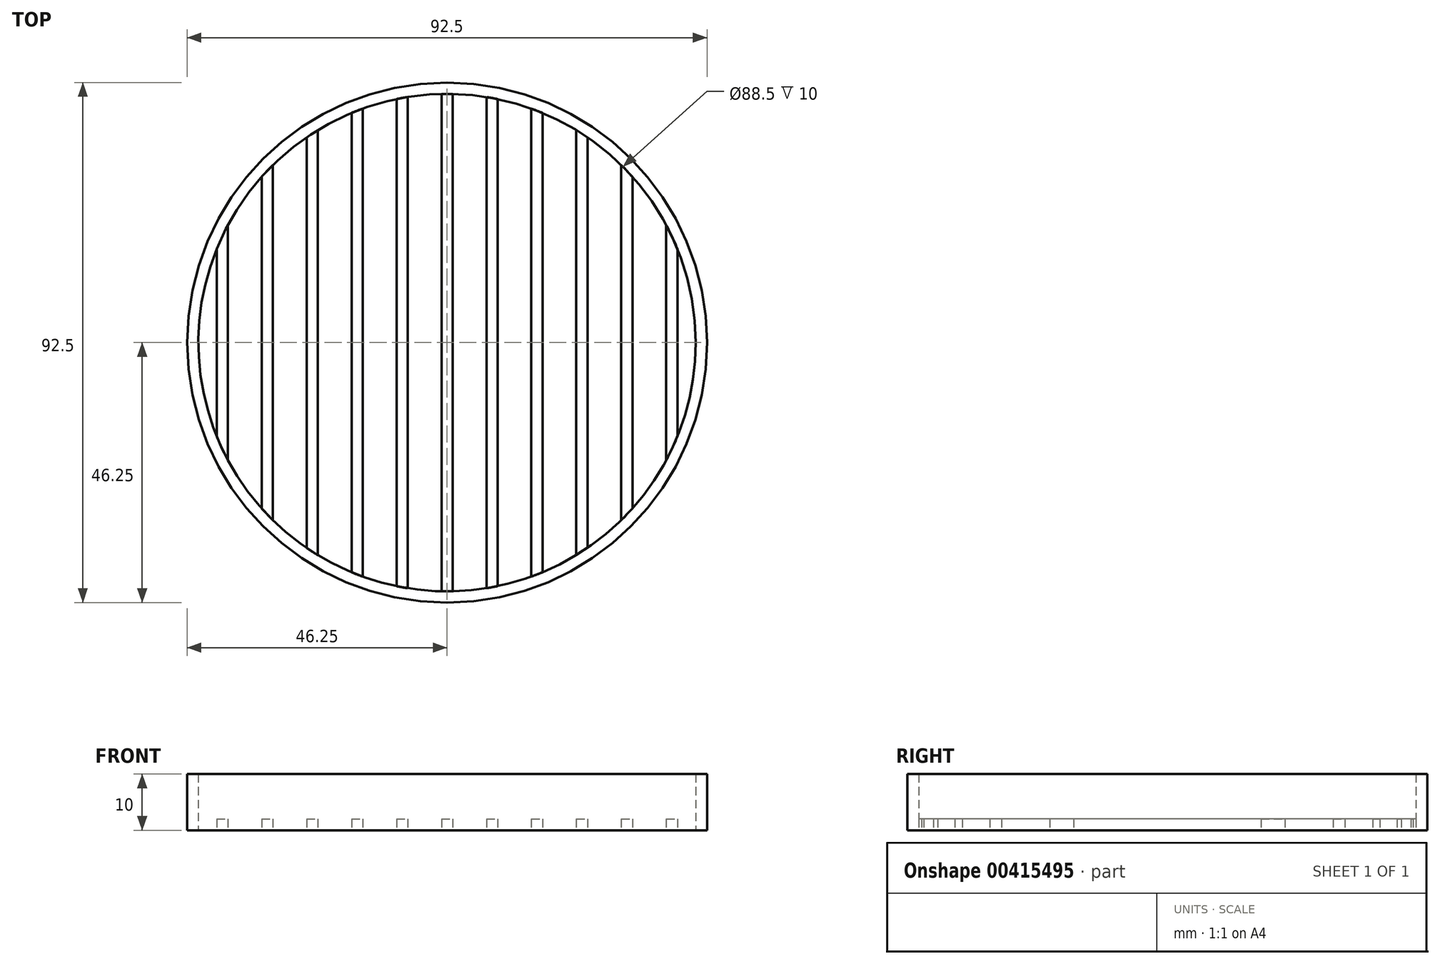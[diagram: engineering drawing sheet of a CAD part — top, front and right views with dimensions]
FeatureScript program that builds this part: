
annotation { "Feature Type Name" : "Feature", "Feature Type Description" : "" }
export const myFeature = defineFeature(function(context is Context, id is Id, definition is map)
    precondition{}
    {
        {
            var Q0;
            Q0=qCreatedBy(makeId("Top.planeOp"),FACE);
            var sketch = newSketch(context, id + "F0", { "sketchPlane" : qUnion([Q0])});
            skCircle(sketch, "E0", {"center": v(0, 0) * mm, "radius": 44.25 * mm});
            skCircle(sketch, "E1", {"center": v(0, 0) * mm, "radius": 46.25 * mm});
            skLineSegment(sketch, "E2", {"start": v(44.25, 0) * mm, "end": v(46.25, 0) * mm, "construction": true});
            skLineSegment(sketch, "E3", {"start": v(0, 44.25) * mm, "end": v(0, -44.25) * mm});
            skLineSegment(sketch, "E4", {"start": v(-1, 46.24) * mm, "end": v(-1, -46.24) * mm});
            skLineSegment(sketch, "E5", {"start": v(1, 38.24) * mm, "end": v(1, -46.24) * mm});
            skLineSegment(sketch, "E6", {"start": v(-1, 6.77) * mm, "end": v(0, 6.77) * mm, "construction": true});
            skLineSegment(sketch, "E7", {"start": v(0, 6.77) * mm, "end": v(1, 6.77) * mm, "construction": true});
            skLineSegment(sketch, "E8", {"start": v(-7, 45.72) * mm, "end": v(-7, -45.72) * mm});
            skLineSegment(sketch, "E9", {"start": v(-7, 0) * mm, "end": v(-1, 0) * mm, "construction": true});
            skLineSegment(sketch, "E10", {"start": v(-9, 45.37) * mm, "end": v(-9, -45.37) * mm});
            skLineSegment(sketch, "E11", {"start": v(-9, 0) * mm, "end": v(-7, 0) * mm, "construction": true});
            skLineSegment(sketch, "E12", {"start": v(-15, 43.75) * mm, "end": v(-15, -43.75) * mm});
            skLineSegment(sketch, "E13", {"start": v(-17, 43.01) * mm, "end": v(-17, -43.01) * mm});
            skLineSegment(sketch, "E14", {"start": v(-15, 0) * mm, "end": v(-9, 0) * mm, "construction": true});
            skLineSegment(sketch, "E15", {"start": v(-17, 0) * mm, "end": v(-15, 0) * mm, "construction": true});
            skLineSegment(sketch, "E16", {"start": v(-23, 40.13) * mm, "end": v(-23, -40.13) * mm});
            skLineSegment(sketch, "E17", {"start": v(-25, 38.91) * mm, "end": v(-25, -38.91) * mm});
            skLineSegment(sketch, "E18", {"start": v(-23, 0) * mm, "end": v(-17, 0) * mm, "construction": true});
            skLineSegment(sketch, "E19", {"start": v(-25, 0) * mm, "end": v(-23, 0) * mm, "construction": true});
            skLineSegment(sketch, "E20", {"start": v(-31, 34.32) * mm, "end": v(-31, -34.32) * mm});
            skLineSegment(sketch, "E21", {"start": v(-33, 32.4) * mm, "end": v(-33, -32.4) * mm});
            skLineSegment(sketch, "E22", {"start": v(-31, 0) * mm, "end": v(-25, 0) * mm, "construction": true});
            skLineSegment(sketch, "E23", {"start": v(-33, 0) * mm, "end": v(-31, 0) * mm, "construction": true});
            skLineSegment(sketch, "E24", {"start": v(7, 45.72) * mm, "end": v(7, -45.72) * mm});
            skLineSegment(sketch, "E25", {"start": v(9, 45.37) * mm, "end": v(9, -45.37) * mm});
            skLineSegment(sketch, "E26", {"start": v(1, 0) * mm, "end": v(7, 0) * mm, "construction": true});
            skPoint(sketch, "E26.startSnap0", {"position": v(7, 0) * mm});
            skLineSegment(sketch, "E27", {"start": v(7, 0) * mm, "end": v(9, 0) * mm, "construction": true});
            skLineSegment(sketch, "E28", {"start": v(15, 43.75) * mm, "end": v(15, -43.75) * mm});
            skLineSegment(sketch, "E29", {"start": v(17, 43.01) * mm, "end": v(17, -43.01) * mm});
            skLineSegment(sketch, "E30", {"start": v(9, 0) * mm, "end": v(15, 0) * mm, "construction": true});
            skLineSegment(sketch, "E31", {"start": v(15, 0) * mm, "end": v(17, 0) * mm, "construction": true});
            skLineSegment(sketch, "E32", {"start": v(23, 40.13) * mm, "end": v(23, -40.13) * mm});
            skLineSegment(sketch, "E33", {"start": v(25, 38.91) * mm, "end": v(25, -38.91) * mm});
            skLineSegment(sketch, "E34", {"start": v(17, 0) * mm, "end": v(23, 0) * mm, "construction": true});
            skLineSegment(sketch, "E35", {"start": v(23, 0) * mm, "end": v(25, 0) * mm, "construction": true});
            skLineSegment(sketch, "E36", {"start": v(31, 34.32) * mm, "end": v(31, -34.32) * mm});
            skLineSegment(sketch, "E37", {"start": v(33, 32.4) * mm, "end": v(33, -32.4) * mm});
            skLineSegment(sketch, "E38", {"start": v(25, 0) * mm, "end": v(31, 0) * mm, "construction": true});
            skLineSegment(sketch, "E39", {"start": v(31, 0) * mm, "end": v(33, 0) * mm, "construction": true});
            skLineSegment(sketch, "E40", {"start": v(-41, 21.4) * mm, "end": v(-41, -21.4) * mm});
            skLineSegment(sketch, "E41", {"start": v(-39, 24.86) * mm, "end": v(-39, -24.86) * mm});
            skLineSegment(sketch, "E42", {"start": v(-39, 0) * mm, "end": v(-33, 0) * mm, "construction": true});
            skLineSegment(sketch, "E43", {"start": v(-41, 0) * mm, "end": v(-39, 0) * mm, "construction": true});
            skLineSegment(sketch, "E44", {"start": v(39, 24.86) * mm, "end": v(39, -24.86) * mm});
            skLineSegment(sketch, "E45", {"start": v(41, 21.4) * mm, "end": v(41, -21.4) * mm});
            skLineSegment(sketch, "E46", {"start": v(33, 0) * mm, "end": v(39, 0) * mm, "construction": true});
            skLineSegment(sketch, "E47", {"start": v(39, 0) * mm, "end": v(41, 0) * mm, "construction": true});
            skLineSegment(sketch, "E48", {"start": v(1, 38.24) * mm, "end": v(1, 46.24) * mm});
            skSolve(sketch);
        }
        {
            var Q0;
            {var subQ0=sQuery(id+"F0.wireOp",EDGE,"E10");var subQ1=sQuery(id+"F0.wireOp",EDGE,"E0");var subQ2=makeQuery(id+"F0.imprint","INTERSECT",VERTEX,{"disambiguationData":[OD(0.0)],"derivedFrom":[subQ1,subQ0]});Q0=makeQuery(id+"F0.imprint","IMPRINT",FACE,{"disambiguationData":[TD([[makeQuery(id+"F0.imprint","IMPRINT",EDGE,{"disambiguationData":[TD([[subQ2,-1.0]])],"derivedFrom":subQ1}),-1.0]])]});}
            var Q1;
            {var subQ0=sQuery(id+"F0.wireOp",EDGE,"E16");var subQ1=sQuery(id+"F0.wireOp",EDGE,"E0");var subQ2=makeQuery(id+"F0.imprint","INTERSECT",VERTEX,{"disambiguationData":[OD(0.0)],"derivedFrom":[subQ1,subQ0]});Q1=makeQuery(id+"F0.imprint","IMPRINT",FACE,{"disambiguationData":[TD([[makeQuery(id+"F0.imprint","IMPRINT",EDGE,{"disambiguationData":[TD([[subQ2,-1.0]])],"derivedFrom":subQ1}),-1.0]])]});}
            var Q2;
            {var subQ0=sQuery(id+"F0.wireOp",EDGE,"E4");var subQ1=sQuery(id+"F0.wireOp",EDGE,"E0");var subQ2=makeQuery(id+"F0.imprint","INTERSECT",VERTEX,{"disambiguationData":[OD(0.0)],"derivedFrom":[subQ1,subQ0]});Q2=makeQuery(id+"F0.imprint","IMPRINT",FACE,{"disambiguationData":[TD([[makeQuery(id+"F0.imprint","IMPRINT",EDGE,{"disambiguationData":[TD([[subQ2,-1.0]])],"derivedFrom":subQ1}),-1.0]])]});}
            var Q3;
            {var subQ0=sQuery(id+"F0.wireOp",EDGE,"E8");var subQ1=sQuery(id+"F0.wireOp",EDGE,"E0");var subQ2=makeQuery(id+"F0.imprint","INTERSECT",VERTEX,{"disambiguationData":[OD(0.0)],"derivedFrom":[subQ1,subQ0]});Q3=makeQuery(id+"F0.imprint","IMPRINT",FACE,{"disambiguationData":[TD([[makeQuery(id+"F0.imprint","IMPRINT",EDGE,{"disambiguationData":[TD([[subQ2,-1.0]])],"derivedFrom":subQ1}),-1.0]])]});}
            var Q4;
            {var subQ3=sQuery(id+"F0.wireOp",EDGE,"E0");var subQ5=makeQuery(id+"F0.imprint","INTERSECT",VERTEX,{"disambiguationData":[OD(0.0)],"derivedFrom":[subQ3,sQuery(id+"F0.wireOp",EDGE,"E3")]});Q4=makeQuery(id+"F0.imprint","IMPRINT",FACE,{"disambiguationData":[TD([[makeQuery(id+"F0.imprint","IMPRINT",EDGE,{"disambiguationData":[TD([[subQ5,1.0]])],"derivedFrom":subQ3}),-1.0]])]});}
            var Q5;
            {var subQ0=sQuery(id+"F0.wireOp",EDGE,"E24");var subQ1=sQuery(id+"F0.wireOp",EDGE,"E0");var subQ2=makeQuery(id+"F0.imprint","INTERSECT",VERTEX,{"disambiguationData":[OD(0.0)],"derivedFrom":[subQ1,subQ0]});Q5=makeQuery(id+"F0.imprint","IMPRINT",FACE,{"disambiguationData":[TD([[makeQuery(id+"F0.imprint","IMPRINT",EDGE,{"disambiguationData":[TD([[subQ2,-1.0]])],"derivedFrom":subQ1}),-1.0]])]});}
            var Q6;
            {var subQ0=sQuery(id+"F0.wireOp",EDGE,"E25");var subQ1=sQuery(id+"F0.wireOp",EDGE,"E0");var subQ2=makeQuery(id+"F0.imprint","INTERSECT",VERTEX,{"disambiguationData":[OD(0.0)],"derivedFrom":[subQ1,subQ0]});Q6=makeQuery(id+"F0.imprint","IMPRINT",FACE,{"disambiguationData":[TD([[makeQuery(id+"F0.imprint","IMPRINT",EDGE,{"disambiguationData":[TD([[subQ2,-1.0]])],"derivedFrom":subQ1}),-1.0]])]});}
            var Q7;
            {var subQ0=sQuery(id+"F0.wireOp",EDGE,"E28");var subQ1=sQuery(id+"F0.wireOp",EDGE,"E0");var subQ2=makeQuery(id+"F0.imprint","INTERSECT",VERTEX,{"disambiguationData":[OD(0.0)],"derivedFrom":[subQ1,subQ0]});Q7=makeQuery(id+"F0.imprint","IMPRINT",FACE,{"disambiguationData":[TD([[makeQuery(id+"F0.imprint","IMPRINT",EDGE,{"disambiguationData":[TD([[subQ2,-1.0]])],"derivedFrom":subQ1}),-1.0]])]});}
            var Q8;
            {var subQ0=sQuery(id+"F0.wireOp",EDGE,"E29");var subQ1=sQuery(id+"F0.wireOp",EDGE,"E0");var subQ2=makeQuery(id+"F0.imprint","INTERSECT",VERTEX,{"disambiguationData":[OD(0.0)],"derivedFrom":[subQ1,subQ0]});Q8=makeQuery(id+"F0.imprint","IMPRINT",FACE,{"disambiguationData":[TD([[makeQuery(id+"F0.imprint","IMPRINT",EDGE,{"disambiguationData":[TD([[subQ2,-1.0]])],"derivedFrom":subQ1}),-1.0]])]});}
            var Q9;
            {var subQ0=sQuery(id+"F0.wireOp",EDGE,"E32");var subQ1=sQuery(id+"F0.wireOp",EDGE,"E0");var subQ2=makeQuery(id+"F0.imprint","INTERSECT",VERTEX,{"disambiguationData":[OD(0.0)],"derivedFrom":[subQ1,subQ0]});Q9=makeQuery(id+"F0.imprint","IMPRINT",FACE,{"disambiguationData":[TD([[makeQuery(id+"F0.imprint","IMPRINT",EDGE,{"disambiguationData":[TD([[subQ2,-1.0]])],"derivedFrom":subQ1}),-1.0]])]});}
            var Q10;
            {var subQ0=sQuery(id+"F0.wireOp",EDGE,"E33");var subQ1=sQuery(id+"F0.wireOp",EDGE,"E0");var subQ2=makeQuery(id+"F0.imprint","INTERSECT",VERTEX,{"disambiguationData":[OD(0.0)],"derivedFrom":[subQ1,subQ0]});Q10=makeQuery(id+"F0.imprint","IMPRINT",FACE,{"disambiguationData":[TD([[makeQuery(id+"F0.imprint","IMPRINT",EDGE,{"disambiguationData":[TD([[subQ2,-1.0]])],"derivedFrom":subQ1}),-1.0]])]});}
            var Q11;
            {var subQ0=sQuery(id+"F0.wireOp",EDGE,"E36");var subQ1=sQuery(id+"F0.wireOp",EDGE,"E0");var subQ2=makeQuery(id+"F0.imprint","INTERSECT",VERTEX,{"disambiguationData":[OD(0.0)],"derivedFrom":[subQ1,subQ0]});Q11=makeQuery(id+"F0.imprint","IMPRINT",FACE,{"disambiguationData":[TD([[makeQuery(id+"F0.imprint","IMPRINT",EDGE,{"disambiguationData":[TD([[subQ2,-1.0]])],"derivedFrom":subQ1}),-1.0]])]});}
            var Q12;
            {var subQ0=sQuery(id+"F0.wireOp",EDGE,"E36");var subQ1=sQuery(id+"F0.wireOp",EDGE,"E0");var subQ2=makeQuery(id+"F0.imprint","INTERSECT",VERTEX,{"disambiguationData":[OD(0.0)],"derivedFrom":[subQ1,subQ0]});Q12=makeQuery(id+"F0.imprint","IMPRINT",FACE,{"disambiguationData":[TD([[makeQuery(id+"F0.imprint","IMPRINT",EDGE,{"disambiguationData":[TD([[subQ2,1.0]])],"derivedFrom":subQ1}),-1.0]])]});}
            var Q13;
            {var subQ0=sQuery(id+"F0.wireOp",EDGE,"E37");var subQ1=sQuery(id+"F0.wireOp",EDGE,"E0");var subQ2=makeQuery(id+"F0.imprint","INTERSECT",VERTEX,{"disambiguationData":[OD(0.0)],"derivedFrom":[subQ1,subQ0]});Q13=makeQuery(id+"F0.imprint","IMPRINT",FACE,{"disambiguationData":[TD([[makeQuery(id+"F0.imprint","IMPRINT",EDGE,{"disambiguationData":[TD([[subQ2,1.0]])],"derivedFrom":subQ1}),-1.0]])]});}
            var Q14;
            {var subQ0=sQuery(id+"F0.wireOp",EDGE,"E20");var subQ1=sQuery(id+"F0.wireOp",EDGE,"E0");var subQ2=makeQuery(id+"F0.imprint","INTERSECT",VERTEX,{"disambiguationData":[OD(0.0)],"derivedFrom":[subQ1,subQ0]});Q14=makeQuery(id+"F0.imprint","IMPRINT",FACE,{"disambiguationData":[TD([[makeQuery(id+"F0.imprint","IMPRINT",EDGE,{"disambiguationData":[TD([[subQ2,-1.0]])],"derivedFrom":subQ1}),-1.0]])]});}
            var Q15;
            {var subQ0=sQuery(id+"F0.wireOp",EDGE,"E21");var subQ1=sQuery(id+"F0.wireOp",EDGE,"E0");var subQ2=makeQuery(id+"F0.imprint","INTERSECT",VERTEX,{"disambiguationData":[OD(0.0)],"derivedFrom":[subQ1,subQ0]});Q15=makeQuery(id+"F0.imprint","IMPRINT",FACE,{"disambiguationData":[TD([[makeQuery(id+"F0.imprint","IMPRINT",EDGE,{"disambiguationData":[TD([[subQ2,-1.0]])],"derivedFrom":subQ1}),-1.0]])]});}
            var Q16;
            {var subQ0=sQuery(id+"F0.wireOp",EDGE,"E36");var subQ1=sQuery(id+"F0.wireOp",EDGE,"E0");var subQ2=makeQuery(id+"F0.imprint","INTERSECT",VERTEX,{"disambiguationData":[OD(1.0)],"derivedFrom":[subQ1,subQ0]});Q16=makeQuery(id+"F0.imprint","IMPRINT",FACE,{"disambiguationData":[TD([[makeQuery(id+"F0.imprint","IMPRINT",EDGE,{"disambiguationData":[TD([[subQ2,-1.0]])],"derivedFrom":subQ1}),-1.0]])]});}
            var Q17;
            {var subQ0=sQuery(id+"F0.wireOp",EDGE,"E33");var subQ1=sQuery(id+"F0.wireOp",EDGE,"E0");var subQ2=makeQuery(id+"F0.imprint","INTERSECT",VERTEX,{"disambiguationData":[OD(1.0)],"derivedFrom":[subQ1,subQ0]});Q17=makeQuery(id+"F0.imprint","IMPRINT",FACE,{"disambiguationData":[TD([[makeQuery(id+"F0.imprint","IMPRINT",EDGE,{"disambiguationData":[TD([[subQ2,-1.0]])],"derivedFrom":subQ1}),-1.0]])]});}
            var Q18;
            {var subQ0=sQuery(id+"F0.wireOp",EDGE,"E32");var subQ1=sQuery(id+"F0.wireOp",EDGE,"E0");var subQ2=makeQuery(id+"F0.imprint","INTERSECT",VERTEX,{"disambiguationData":[OD(1.0)],"derivedFrom":[subQ1,subQ0]});Q18=makeQuery(id+"F0.imprint","IMPRINT",FACE,{"disambiguationData":[TD([[makeQuery(id+"F0.imprint","IMPRINT",EDGE,{"disambiguationData":[TD([[subQ2,-1.0]])],"derivedFrom":subQ1}),-1.0]])]});}
            var Q19;
            {var subQ0=sQuery(id+"F0.wireOp",EDGE,"E29");var subQ1=sQuery(id+"F0.wireOp",EDGE,"E0");var subQ2=makeQuery(id+"F0.imprint","INTERSECT",VERTEX,{"disambiguationData":[OD(1.0)],"derivedFrom":[subQ1,subQ0]});Q19=makeQuery(id+"F0.imprint","IMPRINT",FACE,{"disambiguationData":[TD([[makeQuery(id+"F0.imprint","IMPRINT",EDGE,{"disambiguationData":[TD([[subQ2,-1.0]])],"derivedFrom":subQ1}),-1.0]])]});}
            var Q20;
            {var subQ0=sQuery(id+"F0.wireOp",EDGE,"E28");var subQ1=sQuery(id+"F0.wireOp",EDGE,"E0");var subQ2=makeQuery(id+"F0.imprint","INTERSECT",VERTEX,{"disambiguationData":[OD(1.0)],"derivedFrom":[subQ1,subQ0]});Q20=makeQuery(id+"F0.imprint","IMPRINT",FACE,{"disambiguationData":[TD([[makeQuery(id+"F0.imprint","IMPRINT",EDGE,{"disambiguationData":[TD([[subQ2,-1.0]])],"derivedFrom":subQ1}),-1.0]])]});}
            var Q21;
            {var subQ0=sQuery(id+"F0.wireOp",EDGE,"E25");var subQ1=sQuery(id+"F0.wireOp",EDGE,"E0");var subQ2=makeQuery(id+"F0.imprint","INTERSECT",VERTEX,{"disambiguationData":[OD(1.0)],"derivedFrom":[subQ1,subQ0]});Q21=makeQuery(id+"F0.imprint","IMPRINT",FACE,{"disambiguationData":[TD([[makeQuery(id+"F0.imprint","IMPRINT",EDGE,{"disambiguationData":[TD([[subQ2,-1.0]])],"derivedFrom":subQ1}),-1.0]])]});}
            var Q22;
            {var subQ0=sQuery(id+"F0.wireOp",EDGE,"E24");var subQ1=sQuery(id+"F0.wireOp",EDGE,"E0");var subQ2=makeQuery(id+"F0.imprint","INTERSECT",VERTEX,{"disambiguationData":[OD(1.0)],"derivedFrom":[subQ1,subQ0]});Q22=makeQuery(id+"F0.imprint","IMPRINT",FACE,{"disambiguationData":[TD([[makeQuery(id+"F0.imprint","IMPRINT",EDGE,{"disambiguationData":[TD([[subQ2,-1.0]])],"derivedFrom":subQ1}),-1.0]])]});}
            var Q23;
            {var subQ0=sQuery(id+"F0.wireOp",EDGE,"E5");var subQ1=sQuery(id+"F0.wireOp",EDGE,"E0");var subQ2=makeQuery(id+"F0.imprint","INTERSECT",VERTEX,{"disambiguationData":[OD(1.0)],"derivedFrom":[subQ1,subQ0]});Q23=makeQuery(id+"F0.imprint","IMPRINT",FACE,{"disambiguationData":[TD([[makeQuery(id+"F0.imprint","IMPRINT",EDGE,{"disambiguationData":[TD([[subQ2,-1.0]])],"derivedFrom":subQ1}),-1.0]])]});}
            var Q24;
            {var subQ5=sQuery(id+"F0.wireOp",EDGE,"E0");var subQ6=makeQuery(id+"F0.imprint","INTERSECT",VERTEX,{"disambiguationData":[OD(1.0)],"derivedFrom":[subQ5,sQuery(id+"F0.wireOp",EDGE,"E3")]});Q24=makeQuery(id+"F0.imprint","IMPRINT",FACE,{"disambiguationData":[TD([[makeQuery(id+"F0.imprint","IMPRINT",EDGE,{"disambiguationData":[TD([[subQ6,1.0]])],"derivedFrom":subQ5}),-1.0]])]});}
            var Q25;
            {var subQ0=sQuery(id+"F0.wireOp",EDGE,"E8");var subQ1=sQuery(id+"F0.wireOp",EDGE,"E0");var subQ2=makeQuery(id+"F0.imprint","INTERSECT",VERTEX,{"disambiguationData":[OD(1.0)],"derivedFrom":[subQ1,subQ0]});Q25=makeQuery(id+"F0.imprint","IMPRINT",FACE,{"disambiguationData":[TD([[makeQuery(id+"F0.imprint","IMPRINT",EDGE,{"disambiguationData":[TD([[subQ2,-1.0]])],"derivedFrom":subQ1}),-1.0]])]});}
            var Q26;
            {var subQ0=sQuery(id+"F0.wireOp",EDGE,"E10");var subQ1=sQuery(id+"F0.wireOp",EDGE,"E0");var subQ2=makeQuery(id+"F0.imprint","INTERSECT",VERTEX,{"disambiguationData":[OD(1.0)],"derivedFrom":[subQ1,subQ0]});Q26=makeQuery(id+"F0.imprint","IMPRINT",FACE,{"disambiguationData":[TD([[makeQuery(id+"F0.imprint","IMPRINT",EDGE,{"disambiguationData":[TD([[subQ2,-1.0]])],"derivedFrom":subQ1}),-1.0]])]});}
            var Q27;
            {var subQ0=sQuery(id+"F0.wireOp",EDGE,"E12");var subQ1=sQuery(id+"F0.wireOp",EDGE,"E0");var subQ2=makeQuery(id+"F0.imprint","INTERSECT",VERTEX,{"disambiguationData":[OD(1.0)],"derivedFrom":[subQ1,subQ0]});Q27=makeQuery(id+"F0.imprint","IMPRINT",FACE,{"disambiguationData":[TD([[makeQuery(id+"F0.imprint","IMPRINT",EDGE,{"disambiguationData":[TD([[subQ2,-1.0]])],"derivedFrom":subQ1}),-1.0]])]});}
            var Q28;
            {var subQ0=sQuery(id+"F0.wireOp",EDGE,"E13");var subQ1=sQuery(id+"F0.wireOp",EDGE,"E0");var subQ2=makeQuery(id+"F0.imprint","INTERSECT",VERTEX,{"disambiguationData":[OD(1.0)],"derivedFrom":[subQ1,subQ0]});Q28=makeQuery(id+"F0.imprint","IMPRINT",FACE,{"disambiguationData":[TD([[makeQuery(id+"F0.imprint","IMPRINT",EDGE,{"disambiguationData":[TD([[subQ2,-1.0]])],"derivedFrom":subQ1}),-1.0]])]});}
            var Q29;
            {var subQ0=sQuery(id+"F0.wireOp",EDGE,"E16");var subQ1=sQuery(id+"F0.wireOp",EDGE,"E0");var subQ2=makeQuery(id+"F0.imprint","INTERSECT",VERTEX,{"disambiguationData":[OD(1.0)],"derivedFrom":[subQ1,subQ0]});Q29=makeQuery(id+"F0.imprint","IMPRINT",FACE,{"disambiguationData":[TD([[makeQuery(id+"F0.imprint","IMPRINT",EDGE,{"disambiguationData":[TD([[subQ2,-1.0]])],"derivedFrom":subQ1}),-1.0]])]});}
            var Q30;
            {var subQ0=sQuery(id+"F0.wireOp",EDGE,"E17");var subQ1=sQuery(id+"F0.wireOp",EDGE,"E0");var subQ2=makeQuery(id+"F0.imprint","INTERSECT",VERTEX,{"disambiguationData":[OD(1.0)],"derivedFrom":[subQ1,subQ0]});Q30=makeQuery(id+"F0.imprint","IMPRINT",FACE,{"disambiguationData":[TD([[makeQuery(id+"F0.imprint","IMPRINT",EDGE,{"disambiguationData":[TD([[subQ2,-1.0]])],"derivedFrom":subQ1}),-1.0]])]});}
            var Q31;
            {var subQ0=sQuery(id+"F0.wireOp",EDGE,"E20");var subQ1=sQuery(id+"F0.wireOp",EDGE,"E0");var subQ2=makeQuery(id+"F0.imprint","INTERSECT",VERTEX,{"disambiguationData":[OD(1.0)],"derivedFrom":[subQ1,subQ0]});Q31=makeQuery(id+"F0.imprint","IMPRINT",FACE,{"disambiguationData":[TD([[makeQuery(id+"F0.imprint","IMPRINT",EDGE,{"disambiguationData":[TD([[subQ2,-1.0]])],"derivedFrom":subQ1}),-1.0]])]});}
            var Q32;
            {var subQ0=sQuery(id+"F0.wireOp",EDGE,"E21");var subQ1=sQuery(id+"F0.wireOp",EDGE,"E0");var subQ2=makeQuery(id+"F0.imprint","INTERSECT",VERTEX,{"disambiguationData":[OD(1.0)],"derivedFrom":[subQ1,subQ0]});Q32=makeQuery(id+"F0.imprint","IMPRINT",FACE,{"disambiguationData":[TD([[makeQuery(id+"F0.imprint","IMPRINT",EDGE,{"disambiguationData":[TD([[subQ2,-1.0]])],"derivedFrom":subQ1}),-1.0]])]});}
            var Q33;
            {var subQ0=sQuery(id+"F0.wireOp",EDGE,"E12");var subQ1=sQuery(id+"F0.wireOp",EDGE,"E0");var subQ2=makeQuery(id+"F0.imprint","INTERSECT",VERTEX,{"disambiguationData":[OD(0.0)],"derivedFrom":[subQ1,subQ0]});Q33=makeQuery(id+"F0.imprint","IMPRINT",FACE,{"disambiguationData":[TD([[makeQuery(id+"F0.imprint","IMPRINT",EDGE,{"disambiguationData":[TD([[subQ2,-1.0]])],"derivedFrom":subQ1}),-1.0]])]});}
            var Q34;
            {var subQ0=sQuery(id+"F0.wireOp",EDGE,"E13");var subQ1=sQuery(id+"F0.wireOp",EDGE,"E0");var subQ2=makeQuery(id+"F0.imprint","INTERSECT",VERTEX,{"disambiguationData":[OD(0.0)],"derivedFrom":[subQ1,subQ0]});Q34=makeQuery(id+"F0.imprint","IMPRINT",FACE,{"disambiguationData":[TD([[makeQuery(id+"F0.imprint","IMPRINT",EDGE,{"disambiguationData":[TD([[subQ2,-1.0]])],"derivedFrom":subQ1}),-1.0]])]});}
            var Q35;
            {var subQ0=sQuery(id+"F0.wireOp",EDGE,"E17");var subQ1=sQuery(id+"F0.wireOp",EDGE,"E0");var subQ2=makeQuery(id+"F0.imprint","INTERSECT",VERTEX,{"disambiguationData":[OD(0.0)],"derivedFrom":[subQ1,subQ0]});Q35=makeQuery(id+"F0.imprint","IMPRINT",FACE,{"disambiguationData":[TD([[makeQuery(id+"F0.imprint","IMPRINT",EDGE,{"disambiguationData":[TD([[subQ2,-1.0]])],"derivedFrom":subQ1}),-1.0]])]});}
            var Q36;
            {var subQ0=sQuery(id+"F0.wireOp",EDGE,"E41");var subQ1=sQuery(id+"F0.wireOp",EDGE,"E0");var subQ2=makeQuery(id+"F0.imprint","INTERSECT",VERTEX,{"disambiguationData":[OD(0.0)],"derivedFrom":[subQ1,subQ0]});Q36=makeQuery(id+"F0.imprint","IMPRINT",FACE,{"disambiguationData":[TD([[makeQuery(id+"F0.imprint","IMPRINT",EDGE,{"disambiguationData":[TD([[subQ2,-1.0]])],"derivedFrom":subQ1}),-1.0]])]});}
            var Q37;
            {var subQ0=sQuery(id+"F0.wireOp",EDGE,"E40");var subQ1=sQuery(id+"F0.wireOp",EDGE,"E0");var subQ2=makeQuery(id+"F0.imprint","INTERSECT",VERTEX,{"disambiguationData":[OD(0.0)],"derivedFrom":[subQ1,subQ0]});Q37=makeQuery(id+"F0.imprint","IMPRINT",FACE,{"disambiguationData":[TD([[makeQuery(id+"F0.imprint","IMPRINT",EDGE,{"disambiguationData":[TD([[subQ2,-1.0]])],"derivedFrom":subQ1}),-1.0]])]});}
            var Q38;
            {var subQ0=sQuery(id+"F0.wireOp",EDGE,"E44");var subQ1=sQuery(id+"F0.wireOp",EDGE,"E0");var subQ2=makeQuery(id+"F0.imprint","INTERSECT",VERTEX,{"disambiguationData":[OD(0.0)],"derivedFrom":[subQ1,subQ0]});Q38=makeQuery(id+"F0.imprint","IMPRINT",FACE,{"disambiguationData":[TD([[makeQuery(id+"F0.imprint","IMPRINT",EDGE,{"disambiguationData":[TD([[subQ2,1.0]])],"derivedFrom":subQ1}),-1.0]])]});}
            var Q39;
            {var subQ0=sQuery(id+"F0.wireOp",EDGE,"E45");var subQ1=sQuery(id+"F0.wireOp",EDGE,"E0");var subQ2=makeQuery(id+"F0.imprint","INTERSECT",VERTEX,{"disambiguationData":[OD(0.0)],"derivedFrom":[subQ1,subQ0]});Q39=makeQuery(id+"F0.imprint","IMPRINT",FACE,{"disambiguationData":[TD([[makeQuery(id+"F0.imprint","IMPRINT",EDGE,{"disambiguationData":[TD([[subQ2,1.0]])],"derivedFrom":subQ1}),-1.0]])]});}
            var Q40;
            {var subQ0=sQuery(id+"F0.wireOp",EDGE,"E44");var subQ1=sQuery(id+"F0.wireOp",EDGE,"E0");var subQ2=makeQuery(id+"F0.imprint","INTERSECT",VERTEX,{"disambiguationData":[OD(1.0)],"derivedFrom":[subQ1,subQ0]});Q40=makeQuery(id+"F0.imprint","IMPRINT",FACE,{"disambiguationData":[TD([[makeQuery(id+"F0.imprint","IMPRINT",EDGE,{"disambiguationData":[TD([[subQ2,-1.0]])],"derivedFrom":subQ1}),-1.0]])]});}
            var Q41;
            {var subQ0=sQuery(id+"F0.wireOp",EDGE,"E37");var subQ1=sQuery(id+"F0.wireOp",EDGE,"E0");var subQ2=makeQuery(id+"F0.imprint","INTERSECT",VERTEX,{"disambiguationData":[OD(1.0)],"derivedFrom":[subQ1,subQ0]});Q41=makeQuery(id+"F0.imprint","IMPRINT",FACE,{"disambiguationData":[TD([[makeQuery(id+"F0.imprint","IMPRINT",EDGE,{"disambiguationData":[TD([[subQ2,-1.0]])],"derivedFrom":subQ1}),-1.0]])]});}
            var Q42;
            {var subQ0=sQuery(id+"F0.wireOp",EDGE,"E41");var subQ1=sQuery(id+"F0.wireOp",EDGE,"E0");var subQ2=makeQuery(id+"F0.imprint","INTERSECT",VERTEX,{"disambiguationData":[OD(1.0)],"derivedFrom":[subQ1,subQ0]});Q42=makeQuery(id+"F0.imprint","IMPRINT",FACE,{"disambiguationData":[TD([[makeQuery(id+"F0.imprint","IMPRINT",EDGE,{"disambiguationData":[TD([[subQ2,-1.0]])],"derivedFrom":subQ1}),-1.0]])]});}
            var Q43;
            {var subQ0=sQuery(id+"F0.wireOp",EDGE,"E40");var subQ1=sQuery(id+"F0.wireOp",EDGE,"E0");var subQ2=makeQuery(id+"F0.imprint","INTERSECT",VERTEX,{"disambiguationData":[OD(1.0)],"derivedFrom":[subQ1,subQ0]});Q43=makeQuery(id+"F0.imprint","IMPRINT",FACE,{"disambiguationData":[TD([[makeQuery(id+"F0.imprint","IMPRINT",EDGE,{"disambiguationData":[TD([[subQ2,-1.0]])],"derivedFrom":subQ1}),-1.0]])]});}
            extrude(context, id + "F1", {"entities" : qUnion([Q0, Q1, Q2, Q3, Q4, Q5, Q6, Q7, Q8, Q9, Q10, Q11, Q12, Q13, Q14, Q15, Q16, Q17, Q18, Q19, Q20, Q21, Q22, Q23, Q24, Q25, Q26, Q27, Q28, Q29, Q30, Q31, Q32, Q33, Q34, Q35, Q36, Q37, Q38, Q39, Q40, Q41, Q42, Q43]), "depth" : 10 * mm, "offsetDistance" : 25 * mm});
        }
        {
            var Q0;
            {var subQ0=sQuery(id+"F0.wireOp",EDGE,"E20");var subQ1=sQuery(id+"F0.wireOp",EDGE,"E0");var subQ2=makeQuery(id+"F0.imprint","INTERSECT",VERTEX,{"disambiguationData":[OD(0.0)],"derivedFrom":[subQ1,subQ0]});Q0=makeQuery(id+"F0.imprint","IMPRINT",FACE,{"disambiguationData":[TD([[makeQuery(id+"F0.imprint","IMPRINT",EDGE,{"disambiguationData":[TD([[subQ2,-1.0]])],"derivedFrom":subQ1}),1.0]])]});}
            var Q1;
            {var subQ0=sQuery(id+"F0.wireOp",EDGE,"E16");var subQ1=sQuery(id+"F0.wireOp",EDGE,"E0");var subQ2=makeQuery(id+"F0.imprint","INTERSECT",VERTEX,{"disambiguationData":[OD(0.0)],"derivedFrom":[subQ1,subQ0]});Q1=makeQuery(id+"F0.imprint","IMPRINT",FACE,{"disambiguationData":[TD([[makeQuery(id+"F0.imprint","IMPRINT",EDGE,{"disambiguationData":[TD([[subQ2,-1.0]])],"derivedFrom":subQ1}),1.0]])]});}
            var Q2;
            {var subQ0=sQuery(id+"F0.wireOp",EDGE,"E12");var subQ1=sQuery(id+"F0.wireOp",EDGE,"E0");var subQ2=makeQuery(id+"F0.imprint","INTERSECT",VERTEX,{"disambiguationData":[OD(0.0)],"derivedFrom":[subQ1,subQ0]});Q2=makeQuery(id+"F0.imprint","IMPRINT",FACE,{"disambiguationData":[TD([[makeQuery(id+"F0.imprint","IMPRINT",EDGE,{"disambiguationData":[TD([[subQ2,-1.0]])],"derivedFrom":subQ1}),1.0]])]});}
            var Q3;
            {var subQ0=sQuery(id+"F0.wireOp",EDGE,"E8");var subQ1=sQuery(id+"F0.wireOp",EDGE,"E0");var subQ2=makeQuery(id+"F0.imprint","INTERSECT",VERTEX,{"disambiguationData":[OD(0.0)],"derivedFrom":[subQ1,subQ0]});Q3=makeQuery(id+"F0.imprint","IMPRINT",FACE,{"disambiguationData":[TD([[makeQuery(id+"F0.imprint","IMPRINT",EDGE,{"disambiguationData":[TD([[subQ2,-1.0]])],"derivedFrom":subQ1}),1.0]])]});}
            var Q4;
            {var subQ0=sQuery(id+"F0.wireOp",EDGE,"E3");Q4=makeQuery(id+"F0.imprint","IMPRINT",FACE,{"disambiguationData":[TD([[makeQuery(id+"F0.imprint","IMPRINT",EDGE,{"derivedFrom":subQ0}),-1.0]])]});}
            var Q5;
            {var subQ0=sQuery(id+"F0.wireOp",EDGE,"E25");var subQ1=sQuery(id+"F0.wireOp",EDGE,"E0");var subQ2=makeQuery(id+"F0.imprint","INTERSECT",VERTEX,{"disambiguationData":[OD(0.0)],"derivedFrom":[subQ1,subQ0]});Q5=makeQuery(id+"F0.imprint","IMPRINT",FACE,{"disambiguationData":[TD([[makeQuery(id+"F0.imprint","IMPRINT",EDGE,{"disambiguationData":[TD([[subQ2,-1.0]])],"derivedFrom":subQ1}),1.0]])]});}
            var Q6;
            {var subQ0=sQuery(id+"F0.wireOp",EDGE,"E29");var subQ1=sQuery(id+"F0.wireOp",EDGE,"E0");var subQ2=makeQuery(id+"F0.imprint","INTERSECT",VERTEX,{"disambiguationData":[OD(0.0)],"derivedFrom":[subQ1,subQ0]});Q6=makeQuery(id+"F0.imprint","IMPRINT",FACE,{"disambiguationData":[TD([[makeQuery(id+"F0.imprint","IMPRINT",EDGE,{"disambiguationData":[TD([[subQ2,-1.0]])],"derivedFrom":subQ1}),1.0]])]});}
            var Q7;
            {var subQ0=sQuery(id+"F0.wireOp",EDGE,"E33");var subQ1=sQuery(id+"F0.wireOp",EDGE,"E0");var subQ2=makeQuery(id+"F0.imprint","INTERSECT",VERTEX,{"disambiguationData":[OD(0.0)],"derivedFrom":[subQ1,subQ0]});Q7=makeQuery(id+"F0.imprint","IMPRINT",FACE,{"disambiguationData":[TD([[makeQuery(id+"F0.imprint","IMPRINT",EDGE,{"disambiguationData":[TD([[subQ2,-1.0]])],"derivedFrom":subQ1}),1.0]])]});}
            var Q8;
            {var subQ0=sQuery(id+"F0.wireOp",EDGE,"E36");var subQ1=sQuery(id+"F0.wireOp",EDGE,"E0");var subQ2=makeQuery(id+"F0.imprint","INTERSECT",VERTEX,{"disambiguationData":[OD(0.0)],"derivedFrom":[subQ1,subQ0]});Q8=makeQuery(id+"F0.imprint","IMPRINT",FACE,{"disambiguationData":[TD([[makeQuery(id+"F0.imprint","IMPRINT",EDGE,{"disambiguationData":[TD([[subQ2,1.0]])],"derivedFrom":subQ1}),1.0]])]});}
            var Q9;
            {var subQ0=sQuery(id+"F0.wireOp",EDGE,"E44");var subQ1=sQuery(id+"F0.wireOp",EDGE,"E0");var subQ2=makeQuery(id+"F0.imprint","INTERSECT",VERTEX,{"disambiguationData":[OD(0.0)],"derivedFrom":[subQ1,subQ0]});Q9=makeQuery(id+"F0.imprint","IMPRINT",FACE,{"disambiguationData":[TD([[makeQuery(id+"F0.imprint","IMPRINT",EDGE,{"disambiguationData":[TD([[subQ2,1.0]])],"derivedFrom":subQ1}),1.0]])]});}
            var Q10;
            {var subQ5=sQuery(id+"F0.wireOp",EDGE,"E3");Q10=makeQuery(id+"F0.imprint","IMPRINT",FACE,{"disambiguationData":[TD([[makeQuery(id+"F0.imprint","IMPRINT",EDGE,{"derivedFrom":subQ5}),1.0]])]});}
            var Q11;
            {var subQ0=sQuery(id+"F0.wireOp",EDGE,"E41");var subQ1=sQuery(id+"F0.wireOp",EDGE,"E0");var subQ2=makeQuery(id+"F0.imprint","INTERSECT",VERTEX,{"disambiguationData":[OD(0.0)],"derivedFrom":[subQ1,subQ0]});Q11=makeQuery(id+"F0.imprint","IMPRINT",FACE,{"disambiguationData":[TD([[makeQuery(id+"F0.imprint","IMPRINT",EDGE,{"disambiguationData":[TD([[subQ2,-1.0]])],"derivedFrom":subQ1}),1.0]])]});}
            extrude(context, id + "F2", {"entities" : qUnion([Q0, Q1, Q2, Q3, Q4, Q5, Q6, Q7, Q8, Q9, Q10, Q11]), "operationType" : NewBodyOperationType.ADD, "depth" : 2 * mm, "offsetDistance" : 25 * mm});
        }
    });
